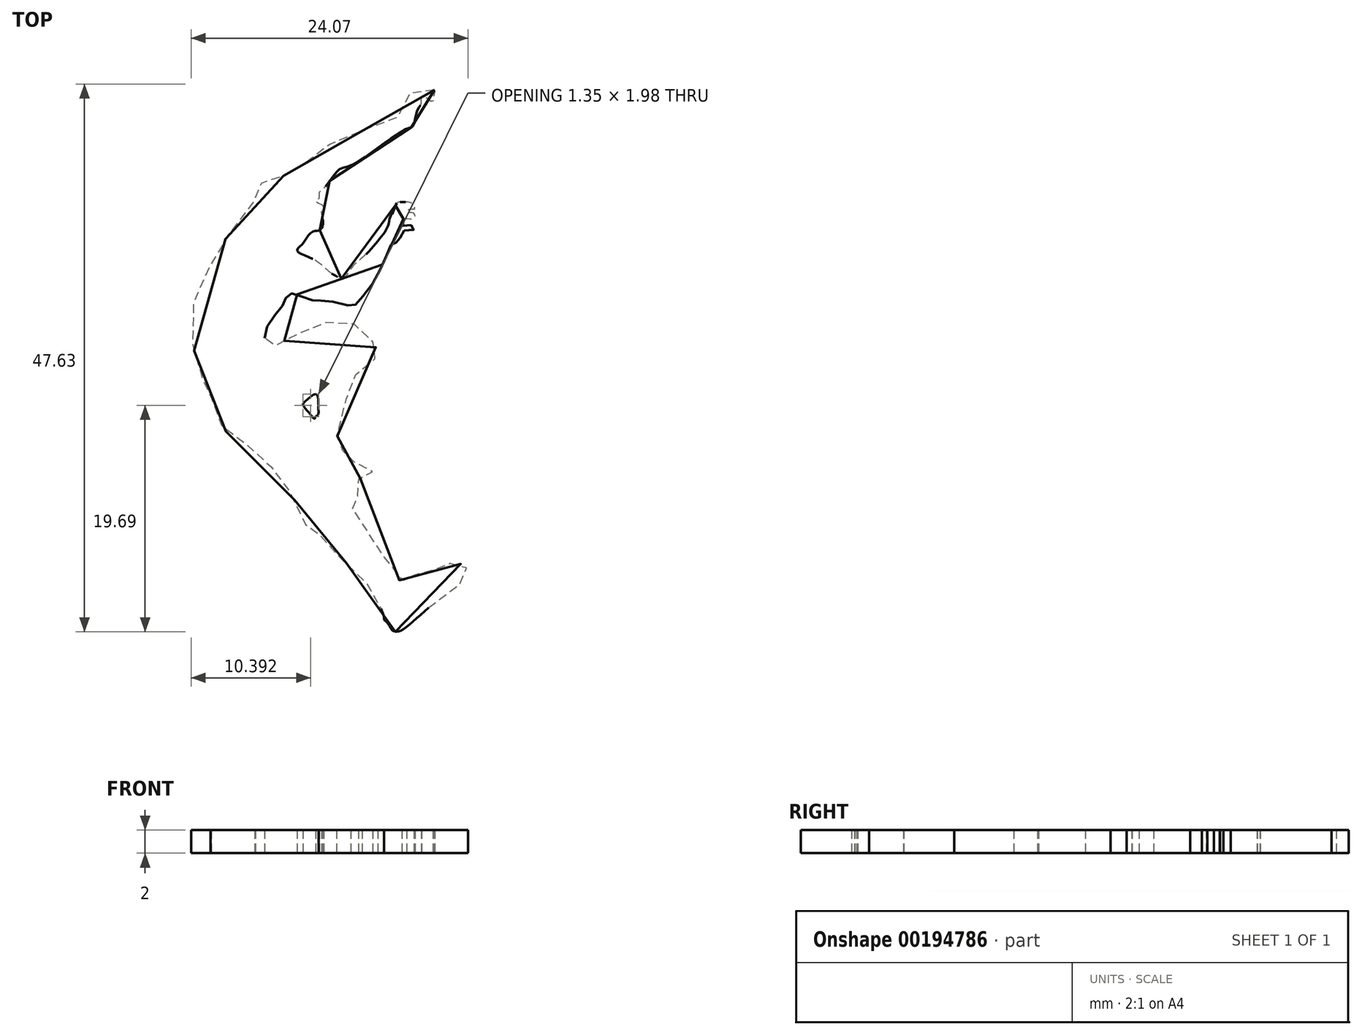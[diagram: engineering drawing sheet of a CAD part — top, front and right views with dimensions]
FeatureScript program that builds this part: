
annotation { "Feature Type Name" : "Feature", "Feature Type Description" : "" }
export const myFeature = defineFeature(function(context is Context, id is Id, definition is map)
    precondition{}
    {
        {
            var Q0;
            Q0=qCreatedBy(makeId("Top.planeOp"),FACE);
            var sketch = newSketch(context, id + "F0", { "sketchPlane" : qUnion([Q0])});
            skFitSpline(sketch, "E0", {"points": [v(-17.82, 62.19) * mm, v(-18.26, 62.6) * mm, v(-19.6, 62.47) * mm, v(-20.06, 61.56) * mm, v(-20.42, 60.89) * mm, v(-20.85, 59.9) * mm, v(-21.2, 59.78) * mm, v(-21.72, 59.64) * mm, v(-23.67, 58.82) * mm, v(-25.69, 58.05) * mm, v(-26.86, 57.47) * mm, v(-27.4, 57.23) * mm, v(-28.35, 56.34) * mm, v(-29.32, 55.6) * mm, v(-30.18, 55) * mm, v(-30.54, 55.02) * mm, v(-30.78, 54.76) * mm, v(-31.46, 54.78) * mm, v(-32.1, 54.54) * mm, v(-32.9, 54.04) * mm, v(-33.26, 53.31) * mm, v(-33.43, 52.83) * mm, v(-33.4, 52.47) * mm, v(-33.74, 52.4) * mm, v(-34.58, 51.13) * mm, v(-36.17, 48.94) * mm, v(-36.99, 47.42) * mm, v(-37.7, 46.25) * mm, v(-38.45, 44.66) * mm, v(-38.88, 43) * mm, v(-38.93, 40.93) * mm, v(-38.6, 39.18) * mm, v(-38.07, 37.76) * mm, v(-37.97, 36.9) * mm, v(-37.59, 35.98) * mm, v(-37.4, 35.64) * mm, v(-37.25, 35.62) * mm, v(-37.27, 34.95) * mm, v(-36.94, 34.06) * mm, v(-36.34, 33.02) * mm, v(-35.42, 31.97) * mm, v(-34.46, 31.46) * mm, v(-33.35, 30.88) * mm, v(-32.54, 29.83) * mm, v(-31.77, 29.18) * mm, v(-31.14, 28.14) * mm, v(-30.6, 27.52) * mm, v(-29.68, 25.9) * mm, v(-29.12, 24.6) * mm, v(-28.7, 24.06) * mm, v(-28.11, 24.03) * mm, v(-27.9, 24) * mm, v(-27.87, 23.7) * mm, v(-27.63, 23.17) * mm, v(-27.08, 22.45) * mm, v(-26.26, 21.75) * mm, v(-24.96, 20.55) * mm, v(-23.6, 19.18) * mm, v(-22.63, 17.95) * mm, v(-22.54, 17.3) * mm, v(-22.42, 16.94) * mm, v(-22.2, 16.34) * mm, v(-22.2, 16.12) * mm, v(-21.84, 15.76) * mm, v(-21.53, 15.26) * mm, v(-21.07, 15.06) * mm, v(-20.32, 15.42) * mm, v(-18.55, 16.96) * mm, v(-16.19, 18.8) * mm, v(-14.99, 19.78) * mm, v(-14.9, 20.16) * mm, v(-15.04, 20.62) * mm, v(-15.35, 20.9) * mm, v(-15.88, 21) * mm, v(-16.62, 20.93) * mm, v(-17.13, 20.55) * mm, v(-17.68, 20.47) * mm, v(-18.2, 20.23) * mm, v(-18.55, 19.94) * mm, v(-19.5, 20) * mm, v(-19.68, 19.75) * mm, v(-20.18, 19.78) * mm, v(-20.47, 19.56) * mm, v(-20.78, 19.49) * mm, v(-21.72, 20.81) * mm, v(-24.96, 25.81) * mm, v(-25.08, 26.03) * mm, v(-24.99, 26.22) * mm, v(-24.72, 26.56) * mm, v(-24.17, 27.42) * mm, v(-24.17, 27.9) * mm, v(-24.41, 28.34) * mm, v(-23.83, 28.4) * mm, v(-23.28, 28.55) * mm, v(-23.23, 29.13) * mm, v(-23.57, 29.47) * mm, v(-24.72, 29.8) * mm, v(-25.2, 30.14) * mm, v(-25.62, 30.4) * mm, v(-25.8, 30.8) * mm, v(-26.07, 30.88) * mm, v(-26.3, 31.33) * mm, v(-26.16, 32.75) * mm, v(-25.53, 35.2) * mm, v(-24.74, 37) * mm, v(-24.66, 37.4) * mm, v(-24.45, 37.68) * mm, v(-23.2, 38.64) * mm, v(-22.8, 39) * mm, v(-22.76, 39.36) * mm, v(-23.12, 40.2) * mm, v(-23.78, 41.25) * mm, v(-25.02, 41.88) * mm, v(-26.4, 41.99) * mm, v(-27.82, 41.83) * mm, v(-28.97, 41.3) * mm, v(-30.45, 40.57) * mm, v(-31.62, 39.97) * mm, v(-32.12, 39.8) * mm, v(-32.46, 40) * mm, v(-32.59, 40.71) * mm, v(-32.09, 42.08) * mm, v(-31.08, 43.34) * mm, v(-30.8, 43.95) * mm, v(-30.45, 44.44) * mm, v(-29.7, 44.37) * mm, v(-28.54, 43.9) * mm, v(-27.87, 43.86) * mm, v(-26.56, 43.74) * mm, v(-24.86, 43.4) * mm, v(-24.61, 43.6) * mm, v(-23.46, 44.94) * mm, v(-22.3, 47.07) * mm, v(-21.64, 48.56) * mm, v(-21.42, 48.92) * mm, v(-21.03, 48.92) * mm, v(-20.81, 49.28) * mm, v(-20.54, 49.91) * mm, v(-19.68, 49.99) * mm, v(-19.66, 50.33) * mm, v(-20.04, 50.4) * mm, v(-20.58, 50.38) * mm, v(-20.6, 50.89) * mm, v(-20.22, 51.01) * mm, v(-19.68, 51) * mm, v(-19.51, 51.21) * mm, v(-19.64, 51.46) * mm, v(-20.02, 51.52) * mm, v(-20.22, 51.52) * mm, v(-20.16, 51.71) * mm, v(-19.75, 51.82) * mm, v(-19.53, 51.84) * mm, v(-19.59, 52.08) * mm, v(-19.9, 52.38) * mm, v(-20.58, 52.44) * mm, v(-21.1, 52.33) * mm, v(-21.37, 51.66) * mm, v(-21.64, 51.2) * mm, v(-21.78, 50.6) * mm, v(-22.09, 49.9) * mm, v(-22.7, 49.1) * mm, v(-23.76, 47.9) * mm, v(-25.13, 46.58) * mm, v(-25.76, 45.75) * mm, v(-26.21, 45.92) * mm, v(-26.7, 46.19) * mm, v(-27.4, 46.76) * mm, v(-28.6, 47.6) * mm, v(-29.74, 48.2) * mm, v(-29.3, 48.8) * mm, v(-28.83, 49.46) * mm, v(-28.25, 49.93) * mm, v(-27.85, 49.95) * mm, v(-27.56, 50.3) * mm, v(-27.51, 50.87) * mm, v(-27.62, 51.5) * mm, v(-27.56, 51.68) * mm, v(-27.44, 51.84) * mm, v(-27.48, 52.07) * mm, v(-27.78, 52.28) * mm, v(-28.1, 52.45) * mm, v(-28.1, 52.57) * mm, v(-27.87, 52.68) * mm, v(-27.83, 53.24) * mm, v(-27.56, 53.52) * mm, v(-26.8, 54.43) * mm, v(-26.22, 55.16) * mm, v(-25.83, 55.39) * mm, v(-25, 55.66) * mm, v(-23.63, 56.52) * mm, v(-21.82, 57.8) * mm, v(-20.8, 58.47) * mm, v(-19.97, 58.9) * mm, v(-19.7, 59.02) * mm, v(-19.5, 59.6) * mm, v(-19.23, 60.57) * mm, v(-19.04, 60.82) * mm, v(-18.95, 61.3) * mm, v(-18.96, 61.53) * mm, v(-18.74, 61.62) * mm, v(-18.47, 61.45) * mm, v(-18.06, 61.22) * mm, v(-17.86, 61.31) * mm, v(-17.93, 61.54) * mm, v(-17.9, 61.63) * mm, v(-17.81, 61.85) * mm, v(-17.82, 62.19) * mm]});
            skFitSpline(sketch, "E1", {"points": [v(-28.16, 35.74) * mm, v(-28.72, 35.4) * mm, v(-29.15, 34.99) * mm, v(-29.26, 34.82) * mm, v(-28.97, 34.4) * mm, v(-28.6, 33.94) * mm, v(-28.25, 33.58) * mm, v(-28.16, 33.79) * mm, v(-27.96, 33.88) * mm, v(-27.92, 34.79) * mm, v(-27.98, 35.62) * mm, v(-28.16, 35.74) * mm]});
            skSolve(sketch);
        }
        {
            var Q0;
            Q0 = qSketchRegion(id + "F0", true);
            extrude(context, id + "F1", {"entities" : qUnion([Q0]), "depth" : 2 * mm});
        }
    });
